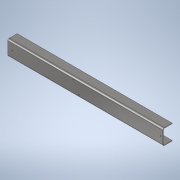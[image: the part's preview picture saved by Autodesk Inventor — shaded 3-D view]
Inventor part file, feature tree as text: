
AUTODESK INVENTOR PART (.ipt)
format: ipt  version: 2020 (Build 240168000, 168)  size: 156,672 bytes
history: native  units: mm
features: sheet_metal_op x4, sketch x4, other x4, projected_geometry x3, hole x2, chamfer x1, reference x1
ambient origin geometry x8: Origin, YZ Plane, XZ Plane, XY Plane, X Axis, Y Axis, Z Axis, Center Point
bodies: Solid1 (feature_tree)
feature tree (19):
  sheet_metal_op  "Face1"
  sheet_metal_op  "Flange1"
  chamfer  "Chamfer1"  Distance=5.0mm
  hole  "Hole1"  [1 undecoded]
  hole  "Hole2"  [1 undecoded]
  sketch  "Sketch1"  dims[d0=3000.0mm]
  other  "Plate1"
  sketch  "Sketch2"  dims[d1=280.0mm]
  other  "Plate2"
  sheet_metal_op  "Bend1"
  sheet_metal_op  "Corner1"
  sketch  "Sketch3"  dims[d2=10.0mm]
  projected_geometry  "Projected Loop1"
  reference  "Reference1"
  sketch  "Sketch4"  dims[d3=10.0mm d4=5.0mm d5=20.0mm d6=10.0mm d7=180.0mm d8=90.0deg d9=20.0mm d10=40.0mm d11=10.0mm d12=10.0mm d13=9.0mm d14=2.0mm d15=45.0deg d16=45.0mm d17=95.0mm d18=105.0mm d19=130.0mm d20=100.0mm d22=18.631mm d23=41.91mm d24=4.0mm d25=2.0mm d26=90.0deg d27=50.41mm d28=20.594885mm d29=100.0mm d30=50.0mm d31=116.0mm d32=351.0mm d33=60.0mm d34=8.376mm d35=10.0mm d36=4.0mm d37=2.0mm d38=90.0deg d39=27.3mm d40=20.594885mm]
  projected_geometry  "Projected Loop2"
  projected_geometry  "Projected Loop3"
  other  "SlipersLåda 211018000.iam"
  other  "SlipersLåda 211018012:1"
note: 2 required parameter values undecoded (feature->parameter linkage not recoverable at this tier; creation-order binding heuristic only, values carry confidence <= 0.55)
